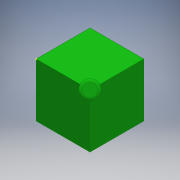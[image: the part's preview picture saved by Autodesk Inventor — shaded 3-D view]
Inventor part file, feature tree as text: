
AUTODESK INVENTOR PART (.ipt)
format: ipt  version: 2018 (Build 220112000, 112)  size: 129,024 bytes
history: native  units: mm
features: sketch x4, extrude x3, plane x2, shell x1, fillet x1, projected_geometry x1
ambient origin geometry x8: Origin, YZ Plane, XZ Plane, XY Plane, X Axis, Y Axis, Z Axis, Center Point
bodies: Solid1 (feature_tree)
feature tree (12):
  extrude  "Extrusion1"  Depth=10.0mm
  shell  "Shell1"  Thickness=10.0mm
  plane  "Work Plane2"
  extrude  "Extrusion2"  Depth=2.0mm
  sketch  "Sketch3"  dims[d6=6.25mm d7=0.0mm d8=4.0mm d9=0.0mm d10=0.5mm]
  extrude  "Extrusion3"  Depth=0.5mm TaperAngle=0.0deg
  fillet  "Fillet1"  Radius=0.5mm
  sketch  "Sketch1"  dims[d0=10.0mm d1=10.0mm d2=10.0mm d3=0.0mm]
  plane  "Work Plane1"
  sketch  "Sketch2"  dims[d4=2.0mm d5=3.0mm]
  sketch  "Sketch4"
  projected_geometry  "Projected Loop1"
